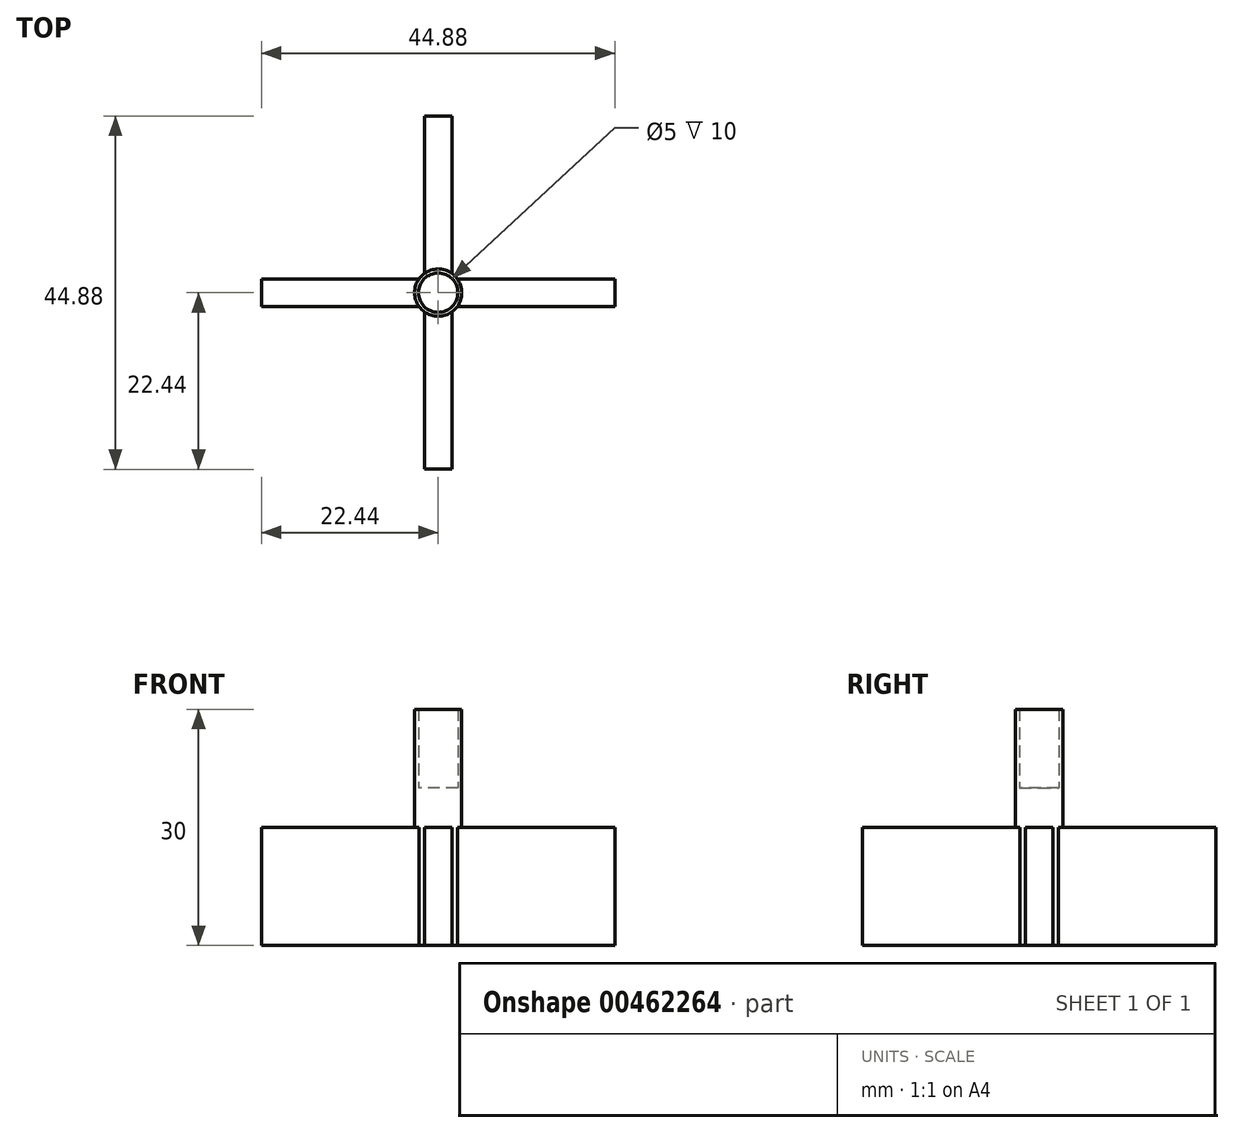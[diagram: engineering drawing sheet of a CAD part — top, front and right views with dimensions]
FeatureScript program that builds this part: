
annotation { "Feature Type Name" : "Feature", "Feature Type Description" : "" }
export const myFeature = defineFeature(function(context is Context, id is Id, definition is map)
    precondition{}
    {
        {
            var Q0;
            Q0=qCreatedBy(makeId("Top.planeOp"),FACE);
            var sketch = newSketch(context, id + "F0", { "sketchPlane" : qUnion([Q0])});
            skCircle(sketch, "E0", {"center": v(0, 0) * mm, "radius": 3 * mm});
            skLineSegment(sketch, "E1", {"start": v(-1.75, 2.44) * mm, "end": v(-1.75, 22.44) * mm});
            skLineSegment(sketch, "E2", {"start": v(1.75, 2.44) * mm, "end": v(1.75, 22.44) * mm});
            skLineSegment(sketch, "E3", {"start": v(-1.75, 22.44) * mm, "end": v(1.75, 22.44) * mm});
            skLineSegment(sketch, "E4", {"start": v(2.44, 1.75) * mm, "end": v(22.44, 1.75) * mm});
            skLineSegment(sketch, "E5", {"start": v(2.44, -1.75) * mm, "end": v(22.44, -1.75) * mm});
            skLineSegment(sketch, "E6", {"start": v(-1.75, -2.44) * mm, "end": v(-1.75, -22.44) * mm});
            skLineSegment(sketch, "E7", {"start": v(1.75, -2.44) * mm, "end": v(1.75, -22.44) * mm});
            skLineSegment(sketch, "E8", {"start": v(-2.44, 1.75) * mm, "end": v(-22.44, 1.75) * mm});
            skLineSegment(sketch, "E9", {"start": v(-2.44, -1.75) * mm, "end": v(-22.44, -1.75) * mm});
            skLineSegment(sketch, "E10", {"start": v(-22.44, -1.75) * mm, "end": v(-22.44, 1.75) * mm});
            skLineSegment(sketch, "E11", {"start": v(-1.75, -22.44) * mm, "end": v(1.75, -22.44) * mm});
            skLineSegment(sketch, "E12", {"start": v(22.44, -1.75) * mm, "end": v(22.44, 1.75) * mm});
            skSolve(sketch);
        }
        {
            var Q0;
            {var subQ0=sQuery(id+"F0.wireOp",EDGE,"E4");Q0=makeQuery(id+"F0.imprint","IMPRINT",FACE,{"disambiguationData":[TD([[makeQuery(id+"F0.imprint","IMPRINT",EDGE,{"derivedFrom":subQ0}),-1.0]])]});}
            var Q1;
            {var subQ0=sQuery(id+"F0.wireOp",EDGE,"E0");var subQ4=makeQuery(id+"F0.imprint","INTERSECT",VERTEX,{"derivedFrom":[subQ0,sQuery(id+"F0.wireOp",EDGE,"E2")]});Q1=makeQuery(id+"F0.imprint","IMPRINT",FACE,{"disambiguationData":[TD([[makeQuery(id+"F0.imprint","IMPRINT",EDGE,{"disambiguationData":[TD([[subQ4,1.0]])],"derivedFrom":subQ0}),1.0]])]});}
            var Q2;
            {var subQ0=sQuery(id+"F0.wireOp",EDGE,"E6");Q2=makeQuery(id+"F0.imprint","IMPRINT",FACE,{"disambiguationData":[TD([[makeQuery(id+"F0.imprint","IMPRINT",EDGE,{"derivedFrom":subQ0}),1.0]])]});}
            var Q3;
            {var subQ0=sQuery(id+"F0.wireOp",EDGE,"E8");Q3=makeQuery(id+"F0.imprint","IMPRINT",FACE,{"disambiguationData":[TD([[makeQuery(id+"F0.imprint","IMPRINT",EDGE,{"derivedFrom":subQ0}),1.0]])]});}
            var Q4;
            {var subQ0=sQuery(id+"F0.wireOp",EDGE,"E1");Q4=makeQuery(id+"F0.imprint","IMPRINT",FACE,{"disambiguationData":[TD([[makeQuery(id+"F0.imprint","IMPRINT",EDGE,{"derivedFrom":subQ0}),-1.0]])]});}
            extrude(context, id + "F1", {"entities" : qUnion([Q0, Q1, Q2, Q3, Q4]), "depth" : 15 * mm});
        }
        {
            var Q0;
            Q0=makeQuery(id+"F1.opExtrude","CAP_FACE",FACE,{"disambiguationData":[OSD([sQuery(id+"F0.wireOp",EDGE,"E0"),sQuery(id+"F0.wireOp",EDGE,"E1"),sQuery(id+"F0.wireOp",EDGE,"E2"),sQuery(id+"F0.wireOp",EDGE,"E3"),sQuery(id+"F0.wireOp",EDGE,"E4"),sQuery(id+"F0.wireOp",EDGE,"E5"),sQuery(id+"F0.wireOp",EDGE,"E6"),sQuery(id+"F0.wireOp",EDGE,"E7"),sQuery(id+"F0.wireOp",EDGE,"E8"),sQuery(id+"F0.wireOp",EDGE,"E9"),sQuery(id+"F0.wireOp",EDGE,"E10"),sQuery(id+"F0.wireOp",EDGE,"E11"),sQuery(id+"F0.wireOp",EDGE,"E12")])],"isStart":false});
            var sketch = newSketch(context, id + "F2", { "sketchPlane" : qUnion([Q0])});
            skCircle(sketch, "E13", {"center": v(0, 0) * mm, "radius": 3 * mm});
            skSolve(sketch);
        }
        {
            var Q0;
            Q0 = qSketchRegion(id + "F2", true);
            extrude(context, id + "F3", {"entities" : qUnion([Q0]), "operationType" : NewBodyOperationType.ADD, "depth" : 5 * mm, "offsetDistance" : 25 * mm});
        }
        {
            var Q0;
            Q0=makeQuery(id+"F3.opExtrude","CAP_FACE",FACE,{"disambiguationData":[OSD([sQuery(id+"F2.wireOp",EDGE,"E13")])],"isStart":false});
            var sketch = newSketch(context, id + "F4", { "sketchPlane" : qUnion([Q0])});
            skCircle(sketch, "E14", {"center": v(0, 0) * mm, "radius": 3 * mm});
            skCircle(sketch, "E15", {"center": v(0, 0) * mm, "radius": 2.5 * mm});
            skSolve(sketch);
        }
        {
            var Q0;
            Q0=makeQuery(id+"F4.imprint","IMPRINT",FACE,{"disambiguationData":[TD([[makeQuery(id+"F4.imprint","IMPRINT",EDGE,{"derivedFrom":sQuery(id+"F4.wireOp",EDGE,"E14")}),1.0]])]});
            extrude(context, id + "F5", {"entities" : qUnion([Q0]), "operationType" : NewBodyOperationType.ADD, "depth" : 10 * mm, "offsetDistance" : 25 * mm});
        }
    });
